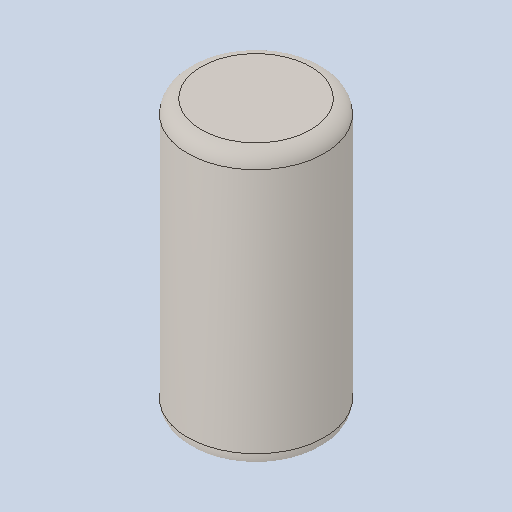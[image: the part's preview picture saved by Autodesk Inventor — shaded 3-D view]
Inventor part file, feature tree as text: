
AUTODESK INVENTOR PART (.ipt)
format: ipt  version: 2023.4 (Build 274418000, 418)  size: 101,888 bytes
history: native  units: in
note: dims shown in document units (in); Inventor stores cm internally (conversion verified against a paired STEP export)
features: fillet x1
ambient origin geometry x8: Origin, YZ Plane, XZ Plane, XY Plane, X Axis, Y Axis, Z Axis, Center Point
bodies: Solid1 (feature_tree)
feature tree (1):
  fillet  "Fillet1"  [1 undecoded]
note: 1 required parameter value undecoded (feature->parameter linkage not recoverable at this tier; creation-order binding heuristic only, values carry confidence <= 0.55)
